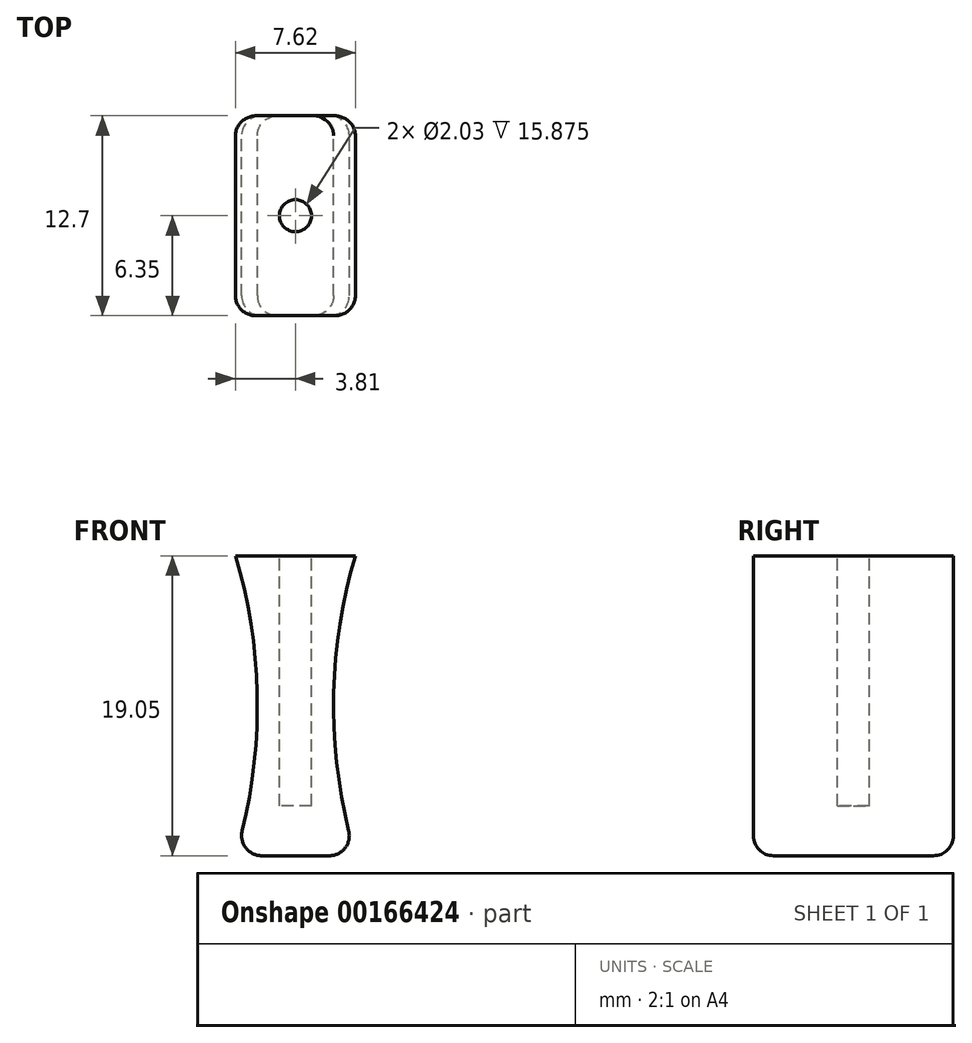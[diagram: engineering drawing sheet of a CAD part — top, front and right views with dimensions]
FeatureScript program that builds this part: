
annotation { "Feature Type Name" : "Feature", "Feature Type Description" : "" }
export const myFeature = defineFeature(function(context is Context, id is Id, definition is map)
    precondition{}
    {
        {
            var Q0;
            Q0=qCreatedBy(makeId("Front.planeOp"),FACE);
            var sketch = newSketch(context, id + "F0", { "sketchPlane" : qUnion([Q0])});
            skLineSegment(sketch, "E0", {"start": v(3.81, 0) * mm, "end": v(0, 0) * mm});
            skLineSegment(sketch, "E1", {"start": v(0, 0) * mm, "end": v(0, 19.05) * mm});
            skLineSegment(sketch, "E2", {"start": v(0, 19.05) * mm, "end": v(3.81, 19.05) * mm});
            skArc(sketch, "E3", {"start": v(3.8, 19.05) * mm, "mid": v(2.42, 9.52) * mm, "end": v(3.8, 0) * mm});
            skLineSegment(sketch, "E4.MirrorCS", {"start": v(-3.81, 0) * mm, "end": v(0, 0) * mm});
            skLineSegment(sketch, "E5.MirrorCS", {"start": v(0, 19.05) * mm, "end": v(-3.81, 19.05) * mm});
            skArc(sketch, "E6.MirrorCS", {"start": v(-3.8, 19.05) * mm, "mid": v(-2.42, 9.52) * mm, "end": v(-3.81, 0) * mm});
            skSolve(sketch);
        }
        {
            var Q0;
            Q0 = qSketchRegion(id + "F0", true);
            extrude(context, id + "F1", {"entities" : qUnion([Q0]), "endBound" : BoundingType.SYMMETRIC, "depth" : 12.7 * mm});
        }
        {
            var Q0;
            Q0=makeQuery(id+"F1.opExtrude","SWEPT_FACE",FACE,{"disambiguationData":[OSD([sQuery(id+"F0.wireOp",EDGE,"E2"),sQuery(id+"F0.wireOp",EDGE,"E5.MirrorCS")])]});
            var sketch = newSketch(context, id + "F2", { "sketchPlane" : qUnion([Q0])});
            skCircle(sketch, "E7", {"center": v(0, 0) * mm, "radius": 1.02 * mm});
            skSolve(sketch);
        }
        {
            var Q0;
            Q0 = qSketchRegion(id + "F2", true);
            extrude(context, id + "F3", {"entities" : qUnion([Q0]), "operationType" : NewBodyOperationType.REMOVE, "oppositeDirection" : true, "depth" : 15.88 * mm});
        }
        {
            var Q0;
            Q0=makeQuery(id+"F1.opExtrude","CAP_EDGE",EDGE,{"disambiguationData":[OSD([sQuery(id+"F0.wireOp",EDGE,"E3")])],"isStart":false});
            var Q1;
            Q1=makeQuery(id+"F1.opExtrude","CAP_EDGE",EDGE,{"disambiguationData":[OSD([sQuery(id+"F0.wireOp",EDGE,"E6.MirrorCS")])],"isStart":false});
            var Q2;
            Q2=makeQuery(id+"F1.opExtrude","CAP_EDGE",EDGE,{"disambiguationData":[OSD([sQuery(id+"F0.wireOp",EDGE,"E0"),sQuery(id+"F0.wireOp",EDGE,"E4.MirrorCS")])],"isStart":false});
            var Q3;
            Q3=makeQuery(id+"F1.opExtrude","SWEPT_EDGE",EDGE,{"disambiguationData":[OSD([sQuery(id+"F0.wireOp",EDGE,"E0"),sQuery(id+"F0.wireOp",EDGE,"E3")])]});
            var Q4;
            Q4=makeQuery(id+"F1.opExtrude","CAP_EDGE",EDGE,{"disambiguationData":[OSD([sQuery(id+"F0.wireOp",EDGE,"E0"),sQuery(id+"F0.wireOp",EDGE,"E4.MirrorCS")])],"isStart":true});
            var Q5;
            Q5=makeQuery(id+"F1.opExtrude","SWEPT_EDGE",EDGE,{"disambiguationData":[OSD([sQuery(id+"F0.wireOp",EDGE,"E4.MirrorCS"),sQuery(id+"F0.wireOp",EDGE,"E6.MirrorCS")])]});
            var Q6;
            Q6=makeQuery(id+"F1.opExtrude","CAP_EDGE",EDGE,{"disambiguationData":[OSD([sQuery(id+"F0.wireOp",EDGE,"E6.MirrorCS")])],"isStart":true});
            var Q7;
            Q7=makeQuery(id+"F1.opExtrude","CAP_EDGE",EDGE,{"disambiguationData":[OSD([sQuery(id+"F0.wireOp",EDGE,"E3")])],"isStart":true});
            fillet(context, id + "F4", {"entities" : qUnion([Q0, Q1, Q2, Q3, Q4, Q5, Q6, Q7]), "radius" : 1.27 * mm, "tangentPropagation" : true, "allowEdgeOverflow" : false});
        }
    });
